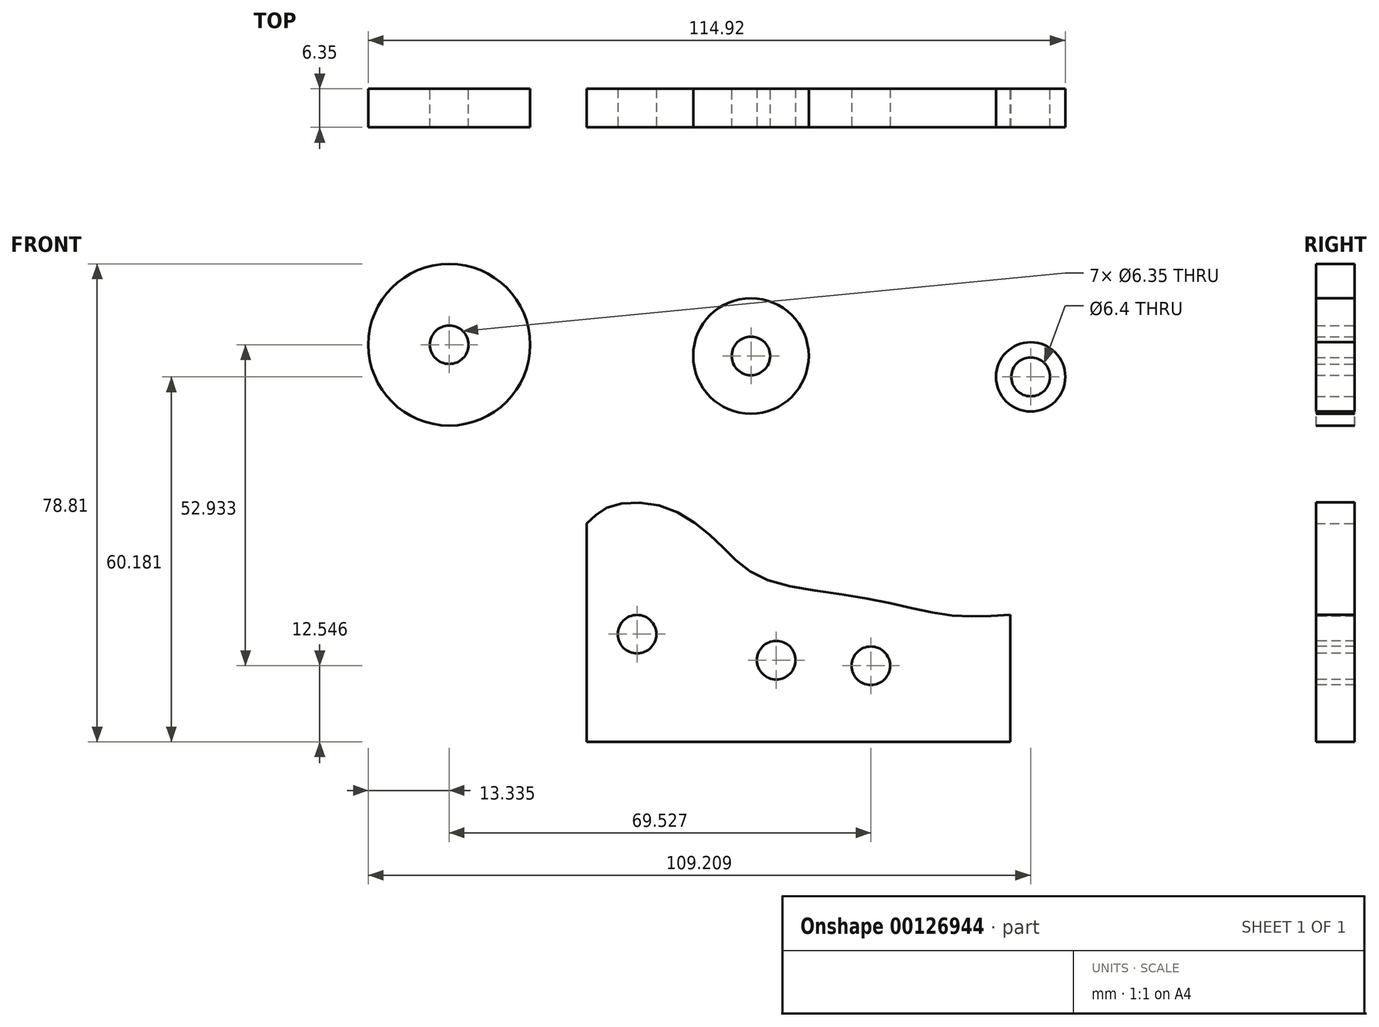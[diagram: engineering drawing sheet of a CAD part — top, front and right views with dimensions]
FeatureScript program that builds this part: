
annotation { "Feature Type Name" : "Feature", "Feature Type Description" : "" }
export const myFeature = defineFeature(function(context is Context, id is Id, definition is map)
    precondition{}
    {
        {
            var Q0;
            Q0=qCreatedBy(makeId("Front.planeOp"),FACE);
            var sketch = newSketch(context, id + "F0", { "sketchPlane" : qUnion([Q0])});
            skLineSegment(sketch, "E0.top", {"start": v(34.93, -20.96) * mm, "end": v(-34.92, -20.96) * mm});
            skLineSegment(sketch, "E0.left", {"start": v(34.93, 0) * mm, "end": v(34.93, -20.96) * mm});
            skLineSegment(sketch, "E0.right", {"start": v(-34.92, 15.07) * mm, "end": v(-34.92, -20.96) * mm});
            skPoint(sketch, "E0.middle", {"position": v(0, 0) * mm});
            skFitSpline(sketch, "E1", {"points": [v(-34.92, 15.07) * mm, v(-31.16, 17.8) * mm, v(-22.26, 17.8) * mm, v(-13.36, 11.99) * mm, v(-6.16, 6.16) * mm, v(10.96, 2.74) * mm, v(24.31, 0) * mm, v(34.93, 0) * mm], "startDerivative": vector(32.96, 32.96) * mm, "endDerivative": vector(72.98, 4.55) * mm});
            skPoint(sketch, "E2.orphan", {"position": v(34.93, 20.95) * mm});
            skPoint(sketch, "E3.orphan", {"position": v(-34.92, 20.96) * mm});
            skSolve(sketch);
        }
        {
            var Q0;
            Q0 = qSketchRegion(id + "F0", true);
            extrude(context, id + "F1", {"entities" : qUnion([Q0]), "depth" : 6.35 * mm});
        }
        {
            var Q0;
            Q0=qCreatedBy(makeId("Front.planeOp"),FACE);
            var sketch = newSketch(context, id + "F2", { "sketchPlane" : qUnion([Q0])});
            skCircle(sketch, "E4", {"center": v(-57.6, 44.52) * mm, "radius": 13.34 * mm});
            skCircle(sketch, "E5", {"center": v(-57.6, 44.52) * mm, "radius": 3.18 * mm});
            skCircle(sketch, "E6", {"center": v(-7.84, 42.67) * mm, "radius": 3.18 * mm});
            skCircle(sketch, "E7", {"center": v(-7.84, 42.67) * mm, "radius": 9.53 * mm});
            skCircle(sketch, "E8", {"center": v(38.28, 39.22) * mm, "radius": 5.72 * mm});
            skCircle(sketch, "E9", {"center": v(38.28, 39.22) * mm, "radius": 3.2 * mm});
            skSolve(sketch);
        }
        {
            var Q0;
            Q0=makeQuery(id+"F2.imprint","IMPRINT",FACE,{"disambiguationData":[TD([[makeQuery(id+"F2.imprint","IMPRINT",EDGE,{"derivedFrom":sQuery(id+"F2.wireOp",EDGE,"E4")}),1.0]])]});
            var Q1;
            Q1=makeQuery(id+"F2.imprint","IMPRINT",FACE,{"disambiguationData":[TD([[makeQuery(id+"F2.imprint","IMPRINT",EDGE,{"derivedFrom":sQuery(id+"F2.wireOp",EDGE,"E6")}),-1.0]])]});
            extrude(context, id + "F3", {"entities" : qUnion([Q0, Q1]), "depth" : 6.35 * mm});
        }
        {
            var Q0;
            Q0 = qSketchRegion(id + "F2", true);
            extrude(context, id + "F4", {"entities" : qUnion([Q0]), "depth" : 6.35 * mm});
        }
        {
            var Q0;
            Q0=makeQuery(id+"F1.opExtrude","CAP_FACE",FACE,{"disambiguationData":[OSD([sQuery(id+"F0.wireOp",EDGE,"E0.top"),sQuery(id+"F0.wireOp",EDGE,"E0.left"),sQuery(id+"F0.wireOp",EDGE,"E0.right"),sQuery(id+"F0.wireOp",EDGE,"E1")])],"isStart":false});
            var sketch = newSketch(context, id + "F5", { "sketchPlane" : qUnion([Q0])});
            skCircle(sketch, "E10", {"center": v(18.66, -6.27) * mm, "radius": 3.18 * mm});
            skSolve(sketch);
        }
        {
            var Q0;
            Q0=makeQuery(id+"F1.opExtrude","CAP_FACE",FACE,{"disambiguationData":[OSD([sQuery(id+"F0.wireOp",EDGE,"E0.top"),sQuery(id+"F0.wireOp",EDGE,"E0.left"),sQuery(id+"F0.wireOp",EDGE,"E0.right"),sQuery(id+"F0.wireOp",EDGE,"E1")])],"isStart":false});
            var sketch = newSketch(context, id + "F6", { "sketchPlane" : qUnion([Q0])});
            skCircle(sketch, "E11", {"center": v(-3.67, -7.5) * mm, "radius": 3.18 * mm});
            skCircle(sketch, "E12", {"center": v(-21.6, -2.94) * mm, "radius": 3.18 * mm});
            skPoint(sketch, "E12.centerSnap0", {"position": v(-34.92, -2.94) * mm});
            skSolve(sketch);
        }
        {
            var Q0;
            Q0=sQuery(id+"F6.wireOp",VERTEX,"E11.center");
            var Q1;
            Q1=makeQuery(id+"F1.opExtrude","SWEPT_BODY",BODY,{"disambiguationData":[OSD([sQuery(id+"F0.wireOp",EDGE,"E0.top"),sQuery(id+"F0.wireOp",EDGE,"E0.left"),sQuery(id+"F0.wireOp",EDGE,"E0.right"),sQuery(id+"F0.wireOp",EDGE,"E1")])]});
            hole(context, id + "F7", {"style" : HoleStyle.SIMPLE, "endStyle" : HoleEndStyle.THROUGH, "holeDiameter" : 6.35 * mm, "locations" : qUnion([Q0]), "scope" : qUnion([Q1]), "isTappedThrough" : true});
        }
        {
            var Q0;
            Q0=makeQuery(id+"F1.opExtrude","CAP_FACE",FACE,{"disambiguationData":[OSD([sQuery(id+"F0.wireOp",EDGE,"E0.top"),sQuery(id+"F0.wireOp",EDGE,"E0.left"),sQuery(id+"F0.wireOp",EDGE,"E0.right"),sQuery(id+"F0.wireOp",EDGE,"E1")])],"isStart":false});
            var sketch = newSketch(context, id + "F8", { "sketchPlane" : qUnion([Q0])});
            skCircle(sketch, "E13", {"center": v(-26.62, -3.21) * mm, "radius": 3.2 * mm});
            skCircle(sketch, "E14", {"center": v(-17.44, -6.27) * mm, "radius": 3.2 * mm});
            skSolve(sketch);
        }
        {
            var Q0;
            Q0=sQuery(id+"F8.wireOp",VERTEX,"E13.center");
            var Q1;
            Q1=makeQuery(id+"F1.opExtrude","SWEPT_BODY",BODY,{"disambiguationData":[OSD([sQuery(id+"F0.wireOp",EDGE,"E0.top"),sQuery(id+"F0.wireOp",EDGE,"E0.left"),sQuery(id+"F0.wireOp",EDGE,"E0.right"),sQuery(id+"F0.wireOp",EDGE,"E1")])]});
            hole(context, id + "F9", {"style" : HoleStyle.SIMPLE, "endStyle" : HoleEndStyle.THROUGH, "holeDiameter" : 6.35 * mm, "locations" : qUnion([Q0]), "scope" : qUnion([Q1]), "isTappedThrough" : true});
        }
        {
            var Q0;
            Q0=makeQuery(id+"F5.imprint","IMPRINT",FACE,{"disambiguationData":[TD([[makeQuery(id+"F5.imprint","IMPRINT",EDGE,{"derivedFrom":sQuery(id+"F5.wireOp",EDGE,"E10")}),-1.0]])]});
            var sketch = newSketch(context, id + "F10", { "sketchPlane" : qUnion([Q0])});
            skCircle(sketch, "E15", {"center": v(11.93, -8.41) * mm, "radius": 3.37 * mm});
            skSolve(sketch);
        }
        {
            var Q0;
            Q0=sQuery(id+"F10.wireOp",VERTEX,"E15.center");
            var Q1;
            Q1=makeQuery(id+"F1.opExtrude","SWEPT_BODY",BODY,{"disambiguationData":[OSD([sQuery(id+"F0.wireOp",EDGE,"E0.top"),sQuery(id+"F0.wireOp",EDGE,"E0.left"),sQuery(id+"F0.wireOp",EDGE,"E0.right"),sQuery(id+"F0.wireOp",EDGE,"E1")])]});
            hole(context, id + "F11", {"style" : HoleStyle.SIMPLE, "endStyle" : HoleEndStyle.THROUGH, "holeDiameter" : 6.35 * mm, "locations" : qUnion([Q0]), "scope" : qUnion([Q1]), "isTappedThrough" : true});
        }
    });
